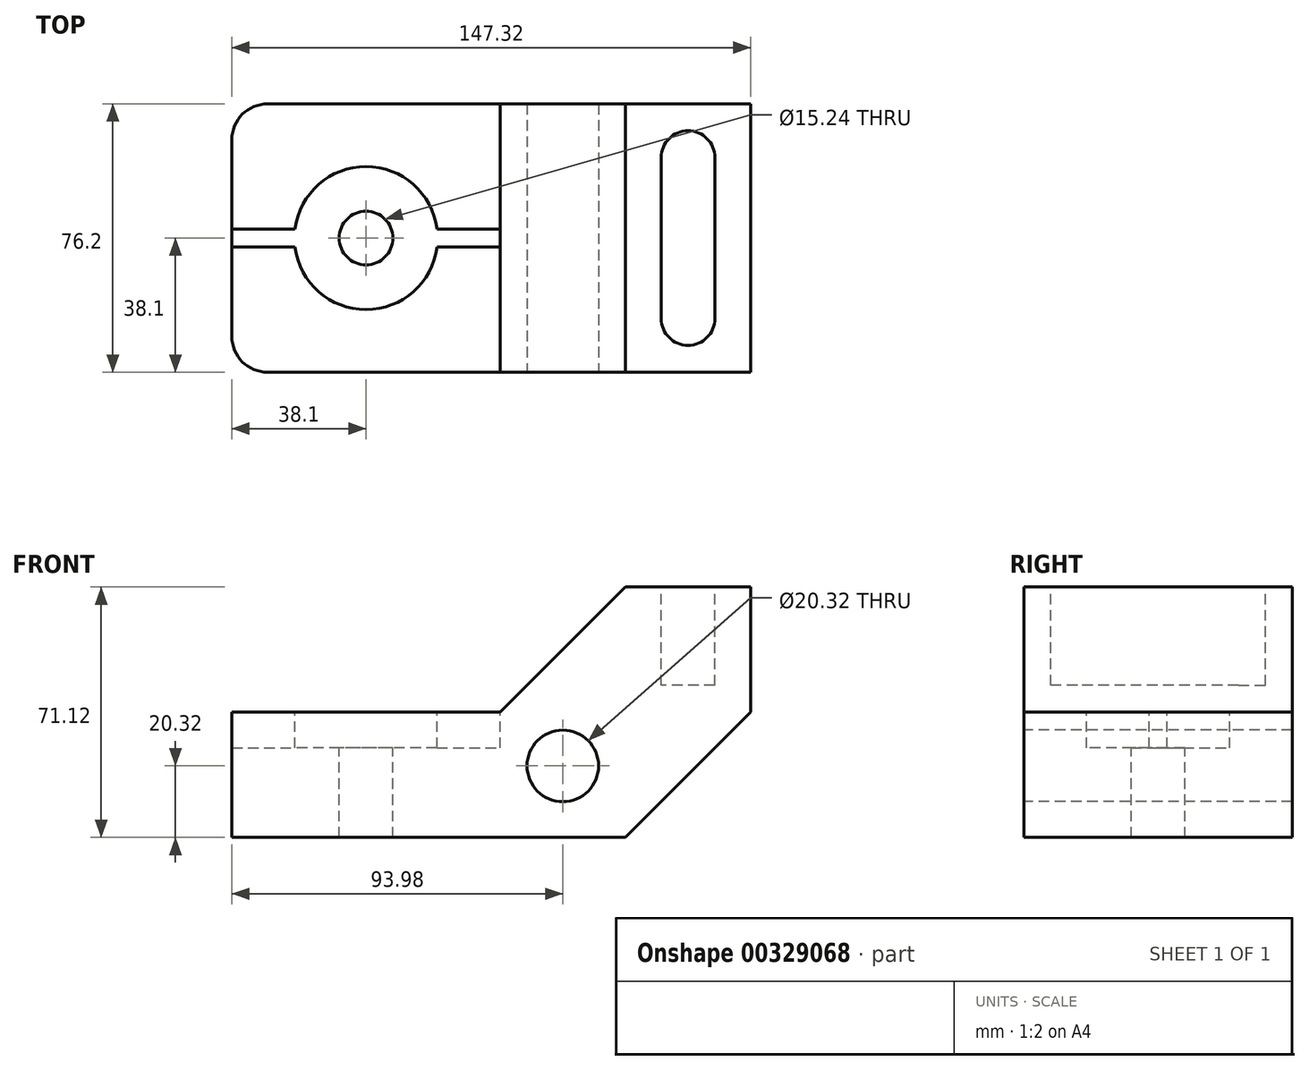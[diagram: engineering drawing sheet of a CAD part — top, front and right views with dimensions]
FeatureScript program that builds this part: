
annotation { "Feature Type Name" : "Feature", "Feature Type Description" : "" }
export const myFeature = defineFeature(function(context is Context, id is Id, definition is map)
    precondition{}
    {
        {
            var Q0;
            Q0=qCreatedBy(makeId("Top.planeOp"),FACE);
            var sketch = newSketch(context, id + "F0", { "sketchPlane" : qUnion([Q0])});
            skLineSegment(sketch, "E0.bottom", {"start": v(0, 0) * mm, "end": v(147.32, 0) * mm});
            skLineSegment(sketch, "E0.top", {"start": v(0, 76.2) * mm, "end": v(147.32, 76.2) * mm});
            skLineSegment(sketch, "E0.left", {"start": v(0, 0) * mm, "end": v(0, 76.2) * mm});
            skLineSegment(sketch, "E0.right", {"start": v(147.32, 0) * mm, "end": v(147.32, 76.2) * mm});
            skSolve(sketch);
        }
        {
            var Q0;
            Q0 = qSketchRegion(id + "F0", true);
            extrude(context, id + "F1", {"entities" : qUnion([Q0]), "depth" : 71.12 * mm});
        }
        {
            var Q0;
            Q0=makeQuery(id+"F1.opExtrude","SWEPT_FACE",FACE,{"disambiguationData":[OSD([sQuery(id+"F0.wireOp",EDGE,"E0.bottom")])]});
            var sketch = newSketch(context, id + "F2", { "sketchPlane" : qUnion([Q0])});
            skLineSegment(sketch, "E1", {"start": v(147.32, 0) * mm, "end": v(147.32, 35.56) * mm});
            skLineSegment(sketch, "E2", {"start": v(147.32, 0) * mm, "end": v(111.76, 0) * mm});
            skLineSegment(sketch, "E3", {"start": v(111.76, 0) * mm, "end": v(147.32, 35.56) * mm});
            skSolve(sketch);
        }
        {
            var Q0;
            Q0 = qSketchRegion(id + "F2", true);
            extrude(context, id + "F3", {"entities" : qUnion([Q0]), "operationType" : NewBodyOperationType.REMOVE, "endBound" : BoundingType.THROUGH_ALL, "oppositeDirection" : true, "depth" : 25.4 * mm});
        }
        {
            var Q0;
            Q0=makeQuery(id+"F1.opExtrude","SWEPT_FACE",FACE,{"disambiguationData":[OSD([sQuery(id+"F0.wireOp",EDGE,"E0.bottom")])]});
            var sketch = newSketch(context, id + "F4", { "sketchPlane" : qUnion([Q0])});
            skLineSegment(sketch, "E4", {"start": v(0, 35.56) * mm, "end": v(76.2, 35.56) * mm});
            skLineSegment(sketch, "E5", {"start": v(111.76, 71.12) * mm, "end": v(76.2, 35.56) * mm});
            skLineSegment(sketch, "E6", {"start": v(0, 71.12) * mm, "end": v(0, 35.56) * mm});
            skLineSegment(sketch, "E7", {"start": v(0, 71.12) * mm, "end": v(111.76, 71.12) * mm});
            skSolve(sketch);
        }
        {
            var Q0;
            Q0 = qSketchRegion(id + "F4", true);
            extrude(context, id + "F5", {"entities" : qUnion([Q0]), "operationType" : NewBodyOperationType.REMOVE, "endBound" : BoundingType.THROUGH_ALL, "oppositeDirection" : true, "depth" : 25.4 * mm});
        }
        {
            var Q0;
            Q0=makeQuery(id+"F1.opExtrude","SWEPT_EDGE",EDGE,{"disambiguationData":[OSD([sQuery(id+"F0.wireOp",EDGE,"E0.bottom"),sQuery(id+"F0.wireOp",EDGE,"E0.left")])]});
            var Q1;
            Q1=makeQuery(id+"F1.opExtrude","SWEPT_EDGE",EDGE,{"disambiguationData":[OSD([sQuery(id+"F0.wireOp",EDGE,"E0.top"),sQuery(id+"F0.wireOp",EDGE,"E0.left")])]});
            fillet(context, id + "F6", {"entities" : qUnion([Q0, Q1]), "radius" : 10.16 * mm, "tangentPropagation" : true, "allowEdgeOverflow" : false});
        }
        {
            var Q0;
            Q0=makeQuery(id+"F5.boolean.opBoolean","COPY",FACE,{"derivedFrom":makeQuery(id+"F5.opExtrude","SWEPT_FACE",FACE,{"disambiguationData":[OSD([sQuery(id+"F4.wireOp",EDGE,"E4")])]})});
            var sketch = newSketch(context, id + "F7", { "sketchPlane" : qUnion([Q0])});
            skLineSegment(sketch, "E8.bottom", {"start": v(0, 40.64) * mm, "end": v(76.2, 40.64) * mm});
            skLineSegment(sketch, "E8.top", {"start": v(0, 35.56) * mm, "end": v(76.2, 35.56) * mm});
            skLineSegment(sketch, "E8.left", {"start": v(0, 40.64) * mm, "end": v(0, 35.56) * mm});
            skLineSegment(sketch, "E8.right", {"start": v(76.2, 40.64) * mm, "end": v(76.2, 35.56) * mm});
            skSolve(sketch);
        }
        {
            var Q0;
            Q0 = qSketchRegion(id + "F7", true);
            extrude(context, id + "F8", {"entities" : qUnion([Q0]), "operationType" : NewBodyOperationType.REMOVE, "oppositeDirection" : true, "depth" : 10.16 * mm});
        }
        {
            var Q0;
            {var subQ1=sQuery(id+"F0.wireOp",EDGE,"E0.bottom");Q0=makeQuery(id+"F8.boolean.opBoolean","SPLIT",FACE,{"disambiguationData":[TD([makeQuery(id+"F1.opExtrude","SWEPT_FACE",FACE,{"disambiguationData":[OSD([subQ1])]})])],"derivedFrom":makeQuery(id+"F5.boolean.opBoolean","COPY",FACE,{"derivedFrom":makeQuery(id+"F5.opExtrude","SWEPT_FACE",FACE,{"disambiguationData":[OSD([sQuery(id+"F4.wireOp",EDGE,"E4")])]})})});}
            var sketch = newSketch(context, id + "F9", { "sketchPlane" : qUnion([Q0])});
            skPoint(sketch, "E9", {"position": v(38.1, 38.1) * mm});
            skSolve(sketch);
        }
        {
            var Q0;
            Q0=sQuery(id+"F9.wireOp",VERTEX,"E9");
            var Q1;
            Q1=makeQuery(id+"F1.opExtrude","SWEPT_BODY",BODY,{"disambiguationData":[OSD([sQuery(id+"F0.wireOp",EDGE,"E0.bottom"),sQuery(id+"F0.wireOp",EDGE,"E0.top"),sQuery(id+"F0.wireOp",EDGE,"E0.left"),sQuery(id+"F0.wireOp",EDGE,"E0.right")])]});
            hole(context, id + "F10", {"style" : HoleStyle.C_BORE, "endStyle" : HoleEndStyle.THROUGH, "holeDiameter" : 15.24 * mm, "cBoreDiameter" : 40.64 * mm, "cBoreDepth" : 10.16 * mm, "tappedDepth" : 12.7 * mm, "tapClearance" : 3, "startFromSketch" : true, "locations" : qUnion([Q0]), "scope" : qUnion([Q1])});
        }
        {
            var Q0;
            Q0=makeQuery(id+"F1.opExtrude","CAP_FACE",FACE,{"disambiguationData":[OSD([sQuery(id+"F0.wireOp",EDGE,"E0.bottom"),sQuery(id+"F0.wireOp",EDGE,"E0.top"),sQuery(id+"F0.wireOp",EDGE,"E0.left"),sQuery(id+"F0.wireOp",EDGE,"E0.right")])],"isStart":false});
            var sketch = newSketch(context, id + "F11", { "sketchPlane" : qUnion([Q0])});
            skArc(sketch, "E10", {"start": v(137.16, 60.96) * mm, "mid": v(129.54, 68.58) * mm, "end": v(121.92, 60.96) * mm});
            skArc(sketch, "E11", {"start": v(121.92, 15.24) * mm, "mid": v(129.54, 7.62) * mm, "end": v(137.16, 15.24) * mm});
            skLineSegment(sketch, "E12", {"start": v(121.92, 60.96) * mm, "end": v(121.92, 15.24) * mm});
            skLineSegment(sketch, "E13", {"start": v(137.16, 60.96) * mm, "end": v(137.16, 15.24) * mm});
            skSolve(sketch);
        }
        {
            var Q0;
            Q0 = qSketchRegion(id + "F11", true);
            extrude(context, id + "F12", {"entities" : qUnion([Q0]), "operationType" : NewBodyOperationType.REMOVE, "oppositeDirection" : true, "depth" : 27.94 * mm});
        }
        {
            var Q0;
            Q0=makeQuery(id+"F1.opExtrude","SWEPT_FACE",FACE,{"disambiguationData":[OSD([sQuery(id+"F0.wireOp",EDGE,"E0.bottom")])]});
            var sketch = newSketch(context, id + "F13", { "sketchPlane" : qUnion([Q0])});
            skPoint(sketch, "E14", {"position": v(93.98, 20.32) * mm});
            skCircle(sketch, "E15", {"center": v(93.98, 20.32) * mm, "radius": 10.16 * mm});
            skSolve(sketch);
        }
        {
            var Q0;
            Q0 = qSketchRegion(id + "F13", true);
            extrude(context, id + "F14", {"entities" : qUnion([Q0]), "operationType" : NewBodyOperationType.REMOVE, "endBound" : BoundingType.THROUGH_ALL, "oppositeDirection" : true, "depth" : 25.4 * mm});
        }
    });
